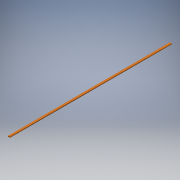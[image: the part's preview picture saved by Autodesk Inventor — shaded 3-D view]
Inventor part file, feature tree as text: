
AUTODESK INVENTOR PART (.ipt)
format: ipt  version: 2019 (Build 230136000, 136)  size: 94,208 bytes
history: native  units: in
note: dims shown in document units (in); Inventor stores cm internally (conversion verified against a paired STEP export)
features: extrude x1, sketch x1
ambient origin geometry x8: Origin, YZ Plane, XZ Plane, XY Plane, X Axis, Y Axis, Z Axis, Center Point
bodies: Solid1 (feature_tree)
feature tree (2):
  extrude  "Extrusion1"  Depth=1.1811in
  sketch  "Sketch1"  dims[d0=2.7559in d1=1.1811in d2=236.2205in d3=0.0in]
